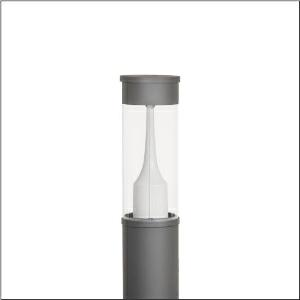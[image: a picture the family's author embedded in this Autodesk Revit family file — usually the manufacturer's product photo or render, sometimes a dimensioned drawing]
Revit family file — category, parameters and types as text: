
# Revit family: city-light_120_iq___p1_0a_5xa5285ff14h_303b
name_source: partatom
category: Lighting Fixtures
units: mm (PartAtom-declared; Revit-internal decimal feet)

## family parameters
Cut with Voids When Loaded = No
Host = Face
Light Source = No
Part Type = Normal
Room Calculation Point = No
Round Connector Dimension = Use Diameter
Shared = No

## types (1)
- --- (1 x LED, 1510 lm, 10.5 W, 3000K)
    Apparent Load = 11 VA
    CIE Flux Codes = 32 61 90 93 100
    Color Rendering = 70
    Color Temperature = 3000K
    Default Elevation = 1800 mm
    Description = City-Light 120 iQ, bollard luminaire, Module 540 iQ-SR, primary light control with 3 zone facetted reflector, of plastic, silver coated, highly specular, structured, primary optical cover: cover, of PMMA, transparent, light distribution: P1.0a, primary light characteristic: strongly asymmetric, LED, High Power LED, rated luminous flux: 1.510lm, luminous efficacy: 144lm/W, light colour: 730, colour temperature: 3000K, control gear: ECG iQ, control: Auto-Match, Temp-Guard, Lumen-Switch, Night-Set, Smart-Wire, Light-Fading, Desk-Remote (wireless, voltage-free reading and setting of iQ features in the workshop via application-optimized NFC function/RFID function), optimised constant luminous flux control (CLO 2.0), Street-Remote, presetting dimming logarithmic, with terminal, 6-pole, max. 2.5mm², mains connection: 230..240V, AC, 50/60Hz, start of lifetime: 11W, end of service life: 11W, reduction: 5W, luminaire housing, cylindrical, of extruded aluminium section, coated, Siteco® metallic grey (DB 702S), length: 1.200mm, diameter: 200mm, Module 540 iQ-SR, traffic white (RAL 9016), equipment: standard, protection rating (complete): IP54, insulation class (complete): insulation class II (safety insulation), certification: CE, ENEC, VDE, packaging unit: 1 piece

Light Distribution: P1.0a
    Height = 500 mm
    Lamp = 1 x LED
    Lamp Light Flux = 1510 lm
    Lamp Power = 10.5 W
    Lamp count = 1
    Length = 200 mm  [stored 0.656168 ft]
    Luminous efficacy = 144 lm/W
    Manufacturer = Siteco
    ModVariant = No
    Model = 5XA5285FF14H
    Mounting Place = Floor
    Mounting Type = Freestanding
    Number of Poles = 1
    OnlyDefault = Yes
    Power Factor = 1
    Product Name = City-Light 120 iQ | P1.0a
    Product group = bollard luminaire
    ProductGroupID = 1304
    Protection Class = Protection class II
    Protection Degree = IP 54
    RLX_Detail_Level = 1
    RLX_Emergency_Light_Flux = 0 lm
    RLX_Emergency_Type = 0
    RLX_Emergency_Type_DB = No
    RlxData = <blob elided: 52609 chars, md5=8e84d74e>
    Socket = socket
    Standby Power = 0 W
    System Light Flux = 1510 lm
    System Power = 11 W
    Type Comments = factory setting: luminous flux: 100 % | dim-lin: 254 | 419 mA
    Type Image = l_1006922.jpg
    URL = http://relux.com
    VarID = @adj_109771
    Voltage = 0 V
    Weight = 0.00 kg
    Width = 0 mm  [stored 0 ft]

note: [stored X ft] marks values corroborated as IEEE doubles in the binary element streams (Revit-internal decimal feet)

## geometry (parser evidence)
native form markers: Blend x4, Sweep x10
no freeform markers — native parametric forms only
